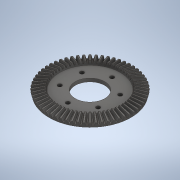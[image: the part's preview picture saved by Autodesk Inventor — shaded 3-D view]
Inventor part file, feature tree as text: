
AUTODESK INVENTOR PART (.ipt)
format: ipt  version: 2020 (Build 240168000, 168)  size: 2,771,968 bytes
history: native  units: in
note: dims shown in document units (in); Inventor stores cm internally (conversion verified against a paired STEP export)
features: extrude x2, sketch x2, imported_body x1
ambient origin geometry x8: Origin, YZ Plane, XZ Plane, XY Plane, X Axis, Y Axis, Z Axis, Center Point
bodies: Solid1 (feature_tree)
feature tree (5):
  extrude  "Extrusion1"  Depth=0.9375in
  extrude  "Extrusion2"  Depth=0.17in
  sketch  "Sketch1"  dims[d0=0.685in d1=0.0in d3=0.9375in]
  sketch  "Sketch2"  dims[d4=1.25in d5=0.17in d6=2.3622in d8=360.0deg d10=0.685in d11=0.0in]
  imported_body  "Base1"
